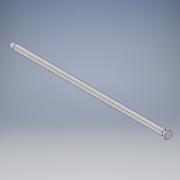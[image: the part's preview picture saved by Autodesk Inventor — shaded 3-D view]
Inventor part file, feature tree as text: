
AUTODESK INVENTOR PART (.ipt)
format: ipt  version: 2017 (Build 210142000, 142)  size: 126,464 bytes
history: native  units: in
note: dims shown in document units (in); Inventor stores cm internally (conversion verified against a paired STEP export)
features: extrude x4, sketch x4
ambient origin geometry x8: Origin, YZ Plane, XZ Plane, XY Plane, X Axis, Y Axis, Z Axis, Center Point
bodies: Solid1 (feature_tree)
feature tree (8):
  extrude  "Extrusion1"  Depth=0.25in
  extrude  "Extrusion2"  TaperAngle=0.0deg  [1 undecoded]
  extrude  "Extrusion3"  Depth=0.125in
  extrude  "Extrusion4"  Depth=0.25in
  sketch  "Sketch1"  dims[d0=10.239in d1=0.25in]
  sketch  "Sketch2"  dims[d2=0.25in d3=0.0in]
  sketch  "Sketch3"  dims[d4=0.125in d5=0.125in]
  sketch  "Sketch4"  dims[d6=0.25in d7=0.25in d8=0.0in d9=0.125in d10=0.125in d11=0.25in d12=0.25in d13=0.0in d14=0.5in d15=0.0625in d16=0.0in]
note: 1 required parameter value undecoded (feature->parameter linkage not recoverable at this tier; creation-order binding heuristic only, values carry confidence <= 0.55)
